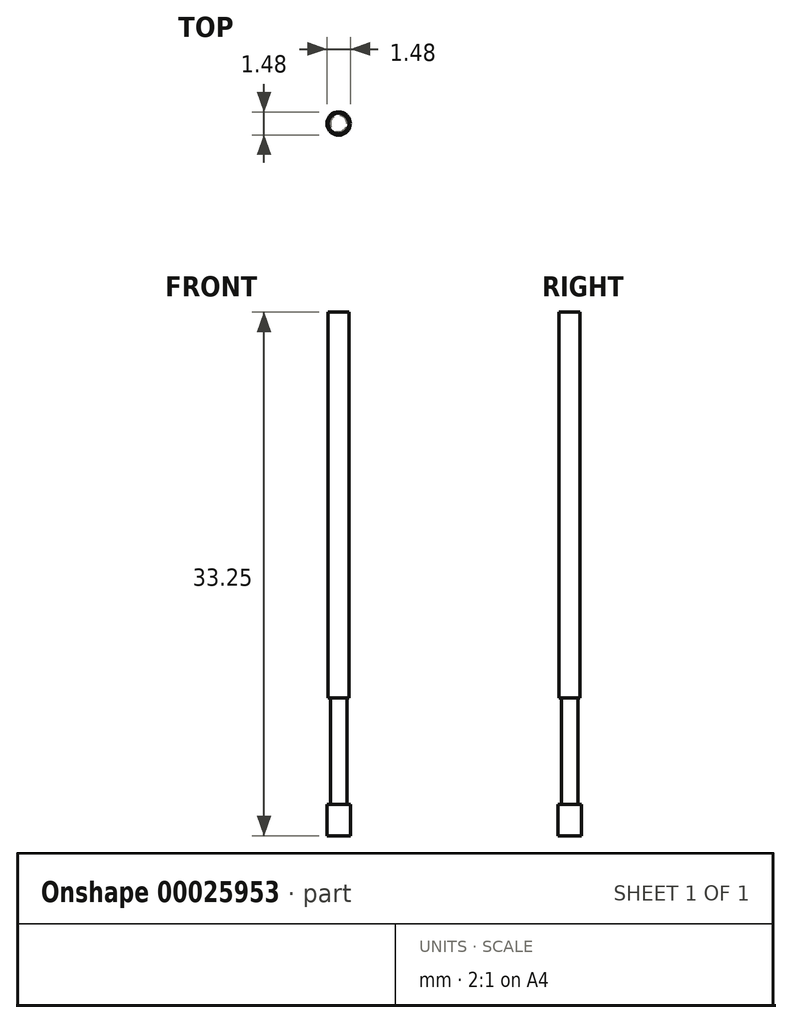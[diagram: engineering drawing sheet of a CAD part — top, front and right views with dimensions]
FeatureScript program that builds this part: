
annotation { "Feature Type Name" : "Feature", "Feature Type Description" : "" }
export const myFeature = defineFeature(function(context is Context, id is Id, definition is map)
    precondition{}
    {
        {
            var Q0;
            Q0=qCreatedBy(makeId("Top.planeOp"),FACE);
            var sketch = newSketch(context, id + "F0", { "sketchPlane" : qUnion([Q0])});
            skCircle(sketch, "E0", {"center": v(0, 0) * mm, "radius": 0.66 * mm});
            skSolve(sketch);
        }
        {
            var Q0;
            Q0 = qSketchRegion(id + "F0", true);
            extrude(context, id + "F1", {"entities" : qUnion([Q0]), "oppositeDirection" : true, "depth" : 24.5 * mm});
        }
        {
            var Q0;
            Q0=makeQuery(id+"F1.opExtrude","CAP_FACE",FACE,{"disambiguationData":[OSD([sQuery(id+"F0.wireOp",EDGE,"E0")])],"isStart":false});
            var sketch = newSketch(context, id + "F2", { "sketchPlane" : qUnion([Q0])});
            skCircle(sketch, "E1", {"center": v(0, 0) * mm, "radius": 0.53 * mm});
            skSolve(sketch);
        }
        {
            var Q0;
            Q0 = qSketchRegion(id + "F2", true);
            extrude(context, id + "F3", {"entities" : qUnion([Q0]), "operationType" : NewBodyOperationType.ADD, "depth" : 6.75 * mm});
        }
        {
            var Q0;
            Q0=makeQuery(id+"F3.opExtrude","CAP_FACE",FACE,{"disambiguationData":[OSD([sQuery(id+"F2.wireOp",EDGE,"E1")])],"isStart":false});
            var sketch = newSketch(context, id + "F4", { "sketchPlane" : qUnion([Q0])});
            skCircle(sketch, "E2", {"center": v(0, 0) * mm, "radius": 0.74 * mm});
            skSolve(sketch);
        }
        {
            var Q0;
            Q0 = qSketchRegion(id + "F4", true);
            extrude(context, id + "F5", {"entities" : qUnion([Q0]), "operationType" : NewBodyOperationType.ADD, "depth" : 2 * mm});
        }
    });
